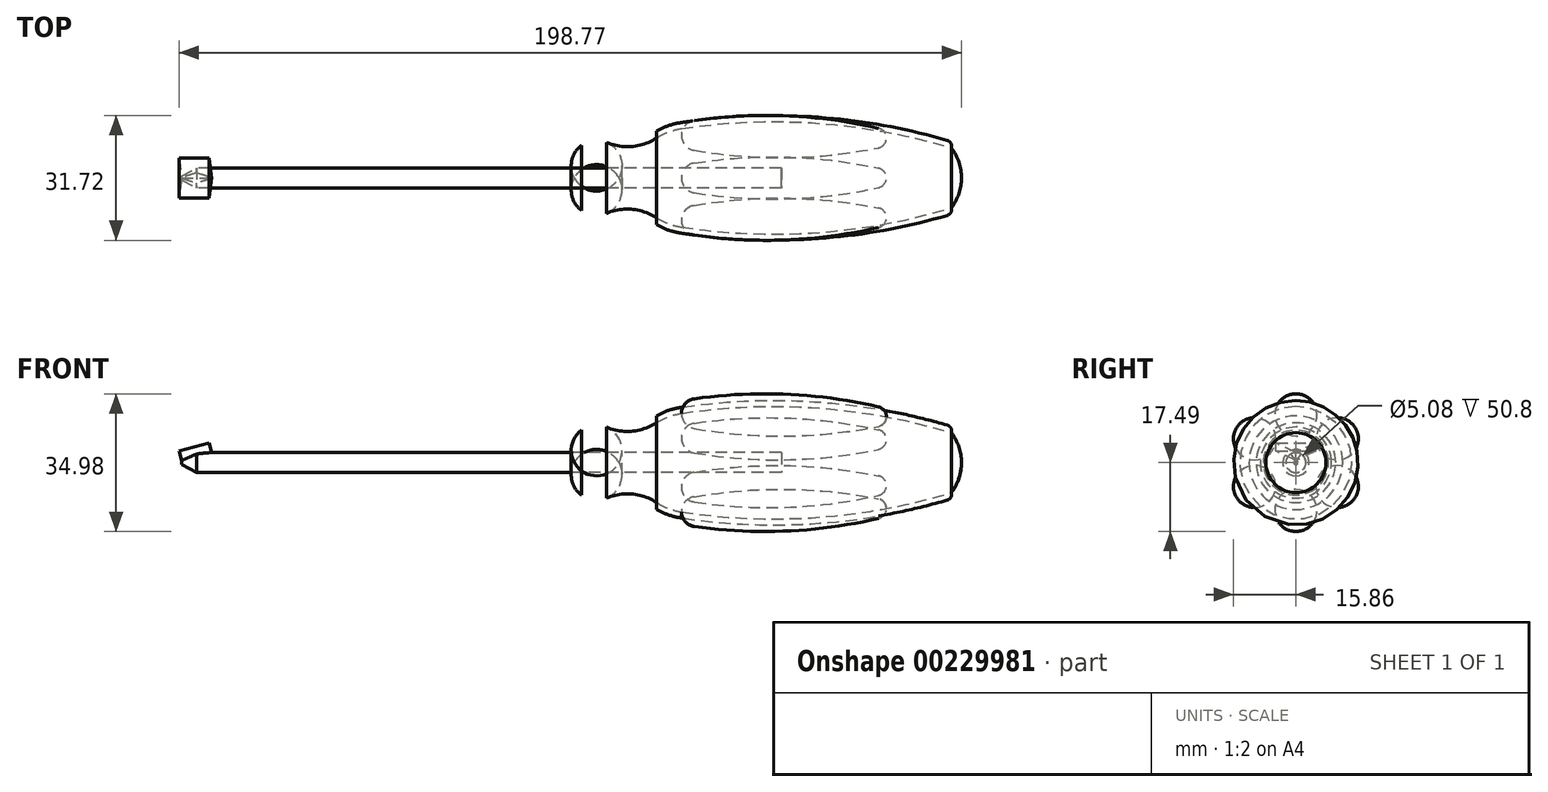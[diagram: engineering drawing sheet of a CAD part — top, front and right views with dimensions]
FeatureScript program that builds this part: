
annotation { "Feature Type Name" : "Feature", "Feature Type Description" : "" }
export const myFeature = defineFeature(function(context is Context, id is Id, definition is map)
    precondition{}
    {
        {
            var Q0;
            Q0=qCreatedBy(makeId("Front.planeOp"),FACE);
            var sketch = newSketch(context, id + "F0", { "sketchPlane" : qUnion([Q0])});
            skLineSegment(sketch, "E0", {"start": v(-101.6, 0) * mm, "end": v(96.52, 0) * mm});
            skLineSegment(sketch, "E1", {"start": v(96.52, 0) * mm, "end": v(117.55, 0) * mm, "construction": true});
            skLineSegment(sketch, "E2", {"start": v(50.8, 2.54) * mm, "end": v(-97.8, 2.54) * mm});
            skLineSegment(sketch, "E3", {"start": v(-101.6, 0.5) * mm, "end": v(-101.6, 0) * mm});
            skLineSegment(sketch, "E4", {"start": v(0, 2.54) * mm, "end": v(0, 8.25) * mm});
            skArc(sketch, "E5", {"start": v(6.35, 9.02) * mm, "mid": v(3.07, 9.48) * mm, "end": v(0, 8.25) * mm});
            skArc(sketch, "E6", {"start": v(6.35, 9.02) * mm, "mid": v(12.84, 7.99) * mm, "end": v(19.05, 10.11) * mm});
            skArc(sketch, "E7", {"start": v(25.4, 12.52) * mm, "mid": v(22.1, 11.65) * mm, "end": v(19.05, 10.11) * mm});
            skArc(sketch, "E8", {"start": v(93.98, 7.62) * mm, "mid": v(59.96, 13.9) * mm, "end": v(25.4, 12.52) * mm});
            skArc(sketch, "E9", {"start": v(96.52, 0) * mm, "mid": v(95.87, 4.02) * mm, "end": v(93.98, 7.62) * mm});
            skArc(sketch, "E10.0", {"start": v(25.17, 14.02) * mm, "mid": v(22.01, 13.24) * mm, "end": v(19.05, 11.9) * mm});
            skArc(sketch, "E10.1", {"start": v(92.95, 9.52) * mm, "mid": v(59.3, 15.46) * mm, "end": v(25.17, 14.02) * mm});
            skLineSegment(sketch, "E11", {"start": v(19.05, 11.9) * mm, "end": v(19.05, 10.11) * mm});
            skArc(sketch, "E12", {"start": v(93.98, 7.62) * mm, "mid": v(93.86, 8.78) * mm, "end": v(92.95, 9.52) * mm});
            skPoint(sketch, "E13.orphan", {"position": v(0, 0) * mm});
            skLineSegment(sketch, "E14", {"start": v(50.8, 2.54) * mm, "end": v(50.8, 0) * mm});
            skLineSegment(sketch, "E15", {"start": v(-101.6, 0.5) * mm, "end": v(-97.8, 2.54) * mm});
            skPoint(sketch, "E16.orphan", {"position": v(-101.6, 2.54) * mm});
            skSolve(sketch);
        }
        {
            var Q0;
            Q0=qCreatedBy(makeId("Front.planeOp"),FACE);
            var sketch = newSketch(context, id + "F1", { "sketchPlane" : qUnion([Q0])});
            skLineSegment(sketch, "E17", {"start": v(25.4, 12.52) * mm, "end": v(77.47, 11.64) * mm});
            skArc(sketch, "E18", {"start": v(28.67, 16.22) * mm, "mid": v(26.35, 14.97) * mm, "end": v(25.4, 12.52) * mm});
            skArc(sketch, "E19", {"start": v(77.47, 11.64) * mm, "mid": v(76.93, 13.25) * mm, "end": v(75.5, 14.16) * mm});
            skArc(sketch, "E20", {"start": v(75.5, 14.16) * mm, "mid": v(52.19, 17.37) * mm, "end": v(28.67, 16.22) * mm});
            skSolve(sketch);
        }
        {
            var Q0;
            Q0=qCreatedBy(makeId("Front.planeOp"),FACE);
            var sketch = newSketch(context, id + "F2", { "sketchPlane" : qUnion([Q0])});
            skLineSegment(sketch, "E21", {"start": v(-101.6, 0.5) * mm, "end": v(-93.98, 2.54) * mm});
            skSolve(sketch);
        }
        {
            var Q0;
            Q0=sQuery(id+"F2.wireOp",VERTEX,"E21.start");
            var Q1;
            Q1=sQuery(id+"F2.wireOp",EDGE,"E21");
            cPlane(context, id + "F3", {"entities" : qUnion([Q0, Q1]), "cplaneType" : CPlaneType.LINE_POINT, "offset" : 25.4 * mm, "width" : 152.4 * mm, "height" : 152.4 * mm});
        }
        {
            var Q0;
            Q0=qCreatedBy(id+"F3.planeOp",FACE);
            var sketch = newSketch(context, id + "F4", { "sketchPlane" : qUnion([Q0])});
            skLineSegment(sketch, "E22", {"start": v(5.08, 29.2) * mm, "end": v(0, 26.67) * mm});
            skLineSegment(sketch, "E23", {"start": v(0, 26.67) * mm, "end": v(-5.08, 29.2) * mm});
            skLineSegment(sketch, "E24", {"start": v(-5.08, 29.2) * mm, "end": v(5.08, 29.2) * mm});
            skLineSegment(sketch, "E25", {"start": v(0, 29.2) * mm, "end": v(0, 26.67) * mm, "construction": true});
            skSolve(sketch);
        }
        {
            var Q0;
            {var subQ0=sQuery(id+"F0.wireOp",EDGE,"E3");Q0=makeQuery(id+"F0.imprint","IMPRINT",FACE,{"disambiguationData":[TD([[makeQuery(id+"F0.imprint","IMPRINT",EDGE,{"derivedFrom":subQ0}),1.0]])]});}
            var Q1;
            Q1=sQuery(id+"F0.wireOp",EDGE,"E1");
            revolve(context, id + "F5", {"entities" : qUnion([Q0]), "axis" : qUnion([Q1]), "revolveType" : RevolveType.FULL});
        }
        {
            var Q0;
            {var subQ0=sQuery(id+"F0.wireOp",EDGE,"E4");Q0=makeQuery(id+"F0.imprint","IMPRINT",FACE,{"disambiguationData":[TD([[makeQuery(id+"F0.imprint","IMPRINT",EDGE,{"derivedFrom":subQ0}),-1.0]])]});}
            var Q1;
            Q1=sQuery(id+"F0.wireOp",EDGE,"E1");
            revolve(context, id + "F6", {"entities" : qUnion([Q0]), "axis" : qUnion([Q1]), "revolveType" : RevolveType.FULL});
        }
        {
            var Q0;
            Q0=makeQuery(id+"F0.imprint","IMPRINT",FACE,{"disambiguationData":[TD([[makeQuery(id+"F0.imprint","IMPRINT",EDGE,{"derivedFrom":sQuery(id+"F0.wireOp",EDGE,"E7")}),-1.0]])]});
            var Q1;
            Q1=sQuery(id+"F0.wireOp",EDGE,"E1");
            revolve(context, id + "F7", {"entities" : qUnion([Q0]), "axis" : qUnion([Q1]), "revolveType" : RevolveType.FULL});
        }
        {
            var Q0;
            Q0=makeQuery(id+"F1.imprint","IMPRINT",FACE,{"disambiguationData":[TD([[makeQuery(id+"F1.imprint","IMPRINT",EDGE,{"derivedFrom":sQuery(id+"F1.wireOp",EDGE,"E17")}),1.0]])]});
            var Q1;
            Q1=sQuery(id+"F1.wireOp",EDGE,"E17");
            revolve(context, id + "F8", {"entities" : qUnion([Q0]), "axis" : qUnion([Q1]), "revolveType" : RevolveType.FULL});
        }
        {
            var Q0;
            Q0=makeQuery(id+"F8.opRevolve","SWEPT_BODY",BODY,{"disambiguationData":[OSD([sQuery(id+"F1.wireOp",EDGE,"E17"),sQuery(id+"F1.wireOp",EDGE,"E18"),sQuery(id+"F1.wireOp",EDGE,"E19"),sQuery(id+"F1.wireOp",EDGE,"E20")])]});
            var Q1;
            Q1=sQuery(id+"F0.wireOp",EDGE,"E1");
            circularPattern(context, id + "F9", {"entities" : qUnion([Q0]), "axis" : qUnion([Q1]), "angle" : 360 * degree, "instanceCount" : 6, "equalSpace" : true});
        }
        {
            var Q0;
            Q0=makeQuery(id+"F6.opRevolve","SWEPT_BODY",BODY,{"disambiguationData":[OSD([sQuery(id+"F0.wireOp",EDGE,"E0"),sQuery(id+"F0.wireOp",EDGE,"E2"),sQuery(id+"F0.wireOp",EDGE,"E4"),sQuery(id+"F0.wireOp",EDGE,"E5"),sQuery(id+"F0.wireOp",EDGE,"E6"),sQuery(id+"F0.wireOp",EDGE,"E7"),sQuery(id+"F0.wireOp",EDGE,"E8"),sQuery(id+"F0.wireOp",EDGE,"E9"),sQuery(id+"F0.wireOp",EDGE,"E14")])]});
            var Q1;
            Q1=makeQuery(id+"F5.opRevolve","SWEPT_BODY",BODY,{"disambiguationData":[OSD([sQuery(id+"F0.wireOp",EDGE,"E0"),sQuery(id+"F0.wireOp",EDGE,"E2"),sQuery(id+"F0.wireOp",EDGE,"E3"),sQuery(id+"F0.wireOp",EDGE,"E14"),sQuery(id+"F0.wireOp",EDGE,"E15")])]});
            var Q2;
            Q2=makeQuery(id+"F7.opRevolve","SWEPT_BODY",BODY,{"disambiguationData":[OSD([sQuery(id+"F0.wireOp",EDGE,"E7"),sQuery(id+"F0.wireOp",EDGE,"E8"),sQuery(id+"F0.wireOp",EDGE,"E10.0"),sQuery(id+"F0.wireOp",EDGE,"E10.1"),sQuery(id+"F0.wireOp",EDGE,"E11"),sQuery(id+"F0.wireOp",EDGE,"E12")])]});
            booleanBodies(context, id + "F10", {"operationType" : BooleanOperationType.SUBTRACTION, "tools" : qUnion([Q0, Q1]), "targets" : qUnion([Q2]), "keepTools" : true});
        }
        {
            var Q0;
            Q0 = qSketchRegion(id + "F4", true);
            var Q1;
            Q1 = qConstructionFilter(qBodyType(qCreatedBy(id + "F2" ,EDGE), BodyType.WIRE), ConstructionObject.NO);
            sweep(context, id + "F11", {"operationType" : NewBodyOperationType.REMOVE, "profiles" : qUnion([Q0]), "path" : qUnion([Q1])});
        }
        {
            var Q0;
            Q0=makeQuery(id+"F4.imprint","IMPRINT",FACE,{"disambiguationData":[TD([[makeQuery(id+"F4.imprint","IMPRINT",EDGE,{"derivedFrom":sQuery(id+"F4.wireOp",EDGE,"E22")}),-1.0]])]});
            var Q1;
            Q1=qConstructionFilter(qBodyType(qCreatedBy(id+"F2",EDGE),BodyType.WIRE),ConstructionObject.NO);
            sweep(context, id + "F12", {"profiles" : qUnion([Q0]), "path" : qUnion([Q1])});
        }
    });
